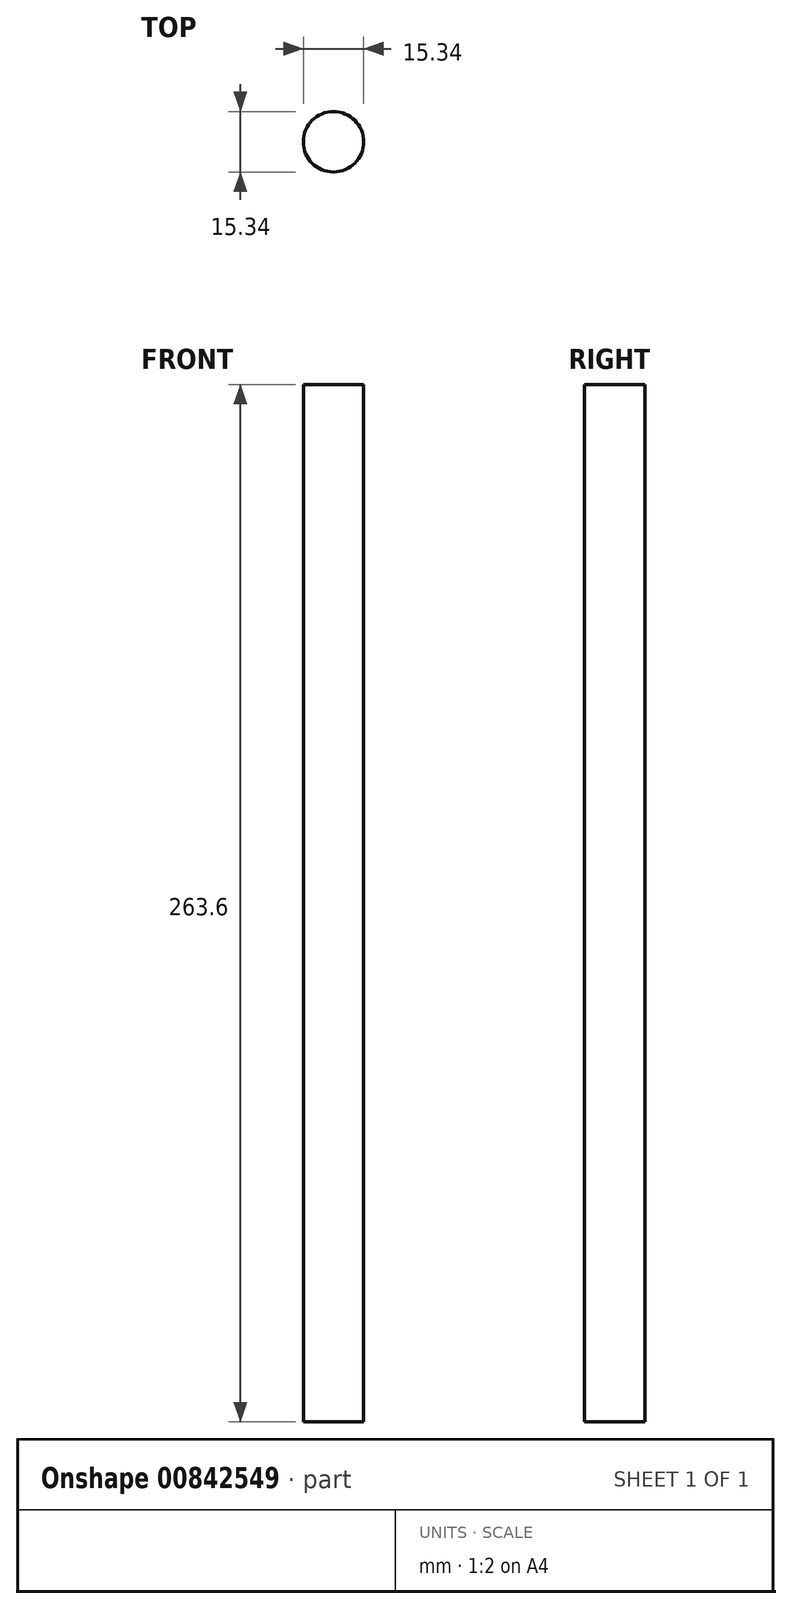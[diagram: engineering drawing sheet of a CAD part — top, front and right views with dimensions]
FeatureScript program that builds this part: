
annotation { "Feature Type Name" : "Feature", "Feature Type Description" : "" }
export const myFeature = defineFeature(function(context is Context, id is Id, definition is map)
    precondition{}
    {
        {
            var Q0;
            Q0=qCreatedBy(makeId("Top.planeOp"),FACE);
            var sketch = newSketch(context, id + "F0", { "sketchPlane" : qUnion([Q0])});
            skCircle(sketch, "E0", {"center": v(0, 0) * mm, "radius": 7.67 * mm});
            skSolve(sketch);
        }
        {
            var Q0;
            Q0 = qSketchRegion(id + "F0", true);
            extrude(context, id + "F1", {"entities" : qUnion([Q0]), "depth" : 263.6 * mm, "offsetDistance" : 25.4 * mm});
        }
    });
